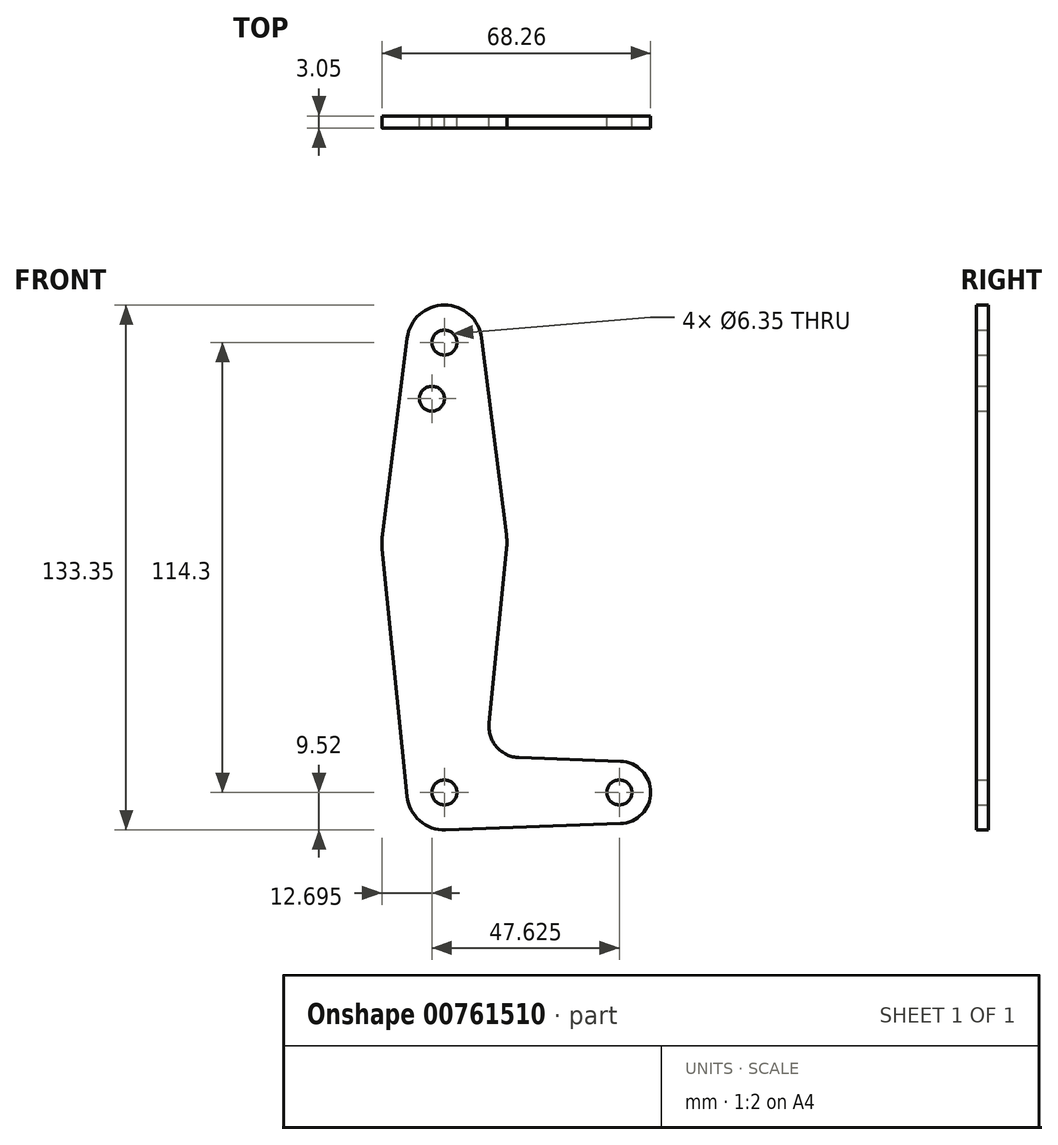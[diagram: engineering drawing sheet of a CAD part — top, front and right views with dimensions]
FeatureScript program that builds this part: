
annotation { "Feature Type Name" : "Feature", "Feature Type Description" : "" }
export const myFeature = defineFeature(function(context is Context, id is Id, definition is map)
    precondition{}
    {
        {
            var Q0;
            Q0=qCreatedBy(makeId("Front.planeOp"),FACE);
            var sketch = newSketch(context, id + "F0", { "sketchPlane" : qUnion([Q0])});
            skLineSegment(sketch, "E0", {"start": v(0, 0) * mm, "end": v(0, 114.3) * mm});
            skLineSegment(sketch, "E1", {"start": v(0, 0) * mm, "end": v(44.45, 0) * mm});
            skCircle(sketch, "E2", {"center": v(0, 0) * mm, "radius": 9.53 * mm});
            skCircle(sketch, "E3", {"center": v(44.45, 0) * mm, "radius": 7.94 * mm});
            skCircle(sketch, "E4", {"center": v(0, 114.3) * mm, "radius": 9.53 * mm});
            skCircle(sketch, "E5", {"center": v(0, 63.5) * mm, "radius": 15.88 * mm});
            skLineSegment(sketch, "E6", {"start": v(-9.45, 115.5) * mm, "end": v(-15.75, 65.48) * mm});
            skLineSegment(sketch, "E7", {"start": v(9.45, 115.5) * mm, "end": v(15.75, 65.48) * mm});
            skLineSegment(sketch, "E8", {"start": v(-15.8, 61.91) * mm, "end": v(-9.48, -0.95) * mm});
            skLineSegment(sketch, "E9", {"start": v(15.8, 61.91) * mm, "end": v(11.34, 17.6) * mm});
            skLineSegment(sketch, "E10", {"start": v(44.73, 7.93) * mm, "end": v(18.97, 8.85) * mm});
            skLineSegment(sketch, "E11", {"start": v(44.73, -7.93) * mm, "end": v(0, -9.53) * mm});
            skCircle(sketch, "E12", {"center": v(0, 114.3) * mm, "radius": 3.18 * mm});
            skCircle(sketch, "E13", {"center": v(-3.18, 100.03) * mm, "radius": 3.18 * mm});
            skCircle(sketch, "E14", {"center": v(0, 0) * mm, "radius": 3.18 * mm});
            skCircle(sketch, "E15", {"center": v(44.45, 0) * mm, "radius": 3.18 * mm});
            skArc(sketch, "E16.filletArc", {"start": v(11.34, 17.6) * mm, "mid": v(13.26, 11.57) * mm, "end": v(18.97, 8.85) * mm});
            skSolve(sketch);
        }
        {
            var Q0;
            Q0 = qSketchRegion(id + "F0", true);
            var Q1;
            {var subQ0=sQuery(id+"F0.wireOp",EDGE,"E14");var subQ1=sQuery(id+"F0.wireOp",EDGE,"E0");var subQ2=makeQuery(id+"F0.imprint","INTERSECT",VERTEX,{"derivedFrom":[subQ1,subQ0]});Q1=makeQuery(id+"F0.imprint","IMPRINT",FACE,{"disambiguationData":[TD([[makeQuery(id+"F0.imprint","IMPRINT",EDGE,{"disambiguationData":[TD([[subQ2,-1.0]])],"derivedFrom":subQ1}),-1.0]])]});}
            extrude(context, id + "F1", {"entities" : qUnion([Q0, Q1]), "depth" : 3.05 * mm, "offsetDistance" : 25.4 * mm});
        }
    });
